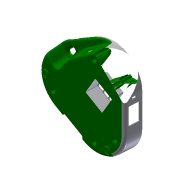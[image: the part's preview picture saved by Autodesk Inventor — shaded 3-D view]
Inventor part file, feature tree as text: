
AUTODESK INVENTOR PART (.ipt)
format: ipt  version: 2016 (Build 200138000, 138)  size: 3,453,440 bytes
history: native  units: in
note: dims shown in document units (in); Inventor stores cm internally (conversion verified against a paired STEP export)
features: extrude x9, sketch x8, projected_geometry x7, reference x5, fillet x3, chamfer x2, other x1, plane x1, pattern_linear x1, imported_body x1
ambient origin geometry x8: Origin, YZ Plane, XZ Plane, XY Plane, X Axis, Y Axis, Z Axis, Center Point
bodies: Solid1 (feature_tree), Solid2 (feature_tree)
feature tree (38):
  other  "bottom_cover-2016-04-29-21"
  sketch  "Sketch1"  dims[d0=0.0709in d1=0.0709in d2=0.3543in]
  plane  "Work Plane1"
  extrude  "Extrusion1"  Depth=0.0709in
  fillet  "Fillet1"  Radius=0.3543in
  extrude  "Extrusion2"  Depth=1.9685in
  extrude  "Extrusion3"  Depth=0.3937in
  extrude  "Extrusion4"  Depth=0.3937in TaperAngle=0.0deg
  chamfer  "Chamfer1"  Distance=3.937in
  chamfer  "Chamfer2"  Distance=0.5118in
  extrude  "Extrusion5"  Depth=0.1575in
  extrude  "Extrusion6"  Depth=0.1575in
  extrude  "Extrusion7"  Depth=0.1575in TaperAngle=30.0deg
  fillet  "Fillet2"  Radius=0.0787in
  pattern_linear  "Rectangular Pattern1"  Spacing1=0.0197in  [1 undecoded]
  fillet  "Fillet3"  Radius=5.9055in
  extrude  "Extrusion8"  TaperAngle=0.0deg  [1 undecoded]
  extrude  "Extrusion9"  TaperAngle=0.0deg  [1 undecoded]
  imported_body  "Base1"
  reference  "Reference1"
  reference  "Reference2"
  sketch  "Sketch6"  dims[d3=0.3543in d4=1.9685in]
  sketch  "Sketch7"  dims[d5=1.5748in d6=0.3937in d7=-0.0069in]
  projected_geometry  "Projected Loop1"
  projected_geometry  "Projected Loop2"
  sketch  "Sketch9"  dims[d8=0.1969in d9=0.3937in d10=0.0in d11=3.937in d12=0.0206in]
  reference  "Reference3"
  reference  "Reference4"
  reference  "Reference5"
  sketch  "Sketch10"  dims[d13=1.6535in]
  projected_geometry  "Projected Loop3"
  sketch  "Sketch11"  dims[d14=2.7559in]
  projected_geometry  "Projected Loop4"
  sketch  "Sketch13"  dims[d16=0.4331in]
  projected_geometry  "Projected Loop5"
  projected_geometry  "Projected Loop6"
  sketch  "Sketch14"  dims[d17=0.2165in d18=0.5118in d19=0.0787in d24=0.1969in d25=-0.0344in d26=0.0787in d27=0.0787in d28=30.0deg d29=0.0787in d30=0.0787in d31=30.0deg d32=0.0197in d33=5.9055in d35=0.0in d36=0.0in d37=3.3858in d38=3.3858in d39=0.2362in d40=0.0787in d41=1.9685in d42=-0.0069in d43=3.189in d44=3.189in d45=0.0787in d46=0.0787in d47=1.8504in d48=-0.0069in d49=0.1181in d50=0.1181in d51=0.9055in d52=0.9055in d53=2.7559in d54=-0.0069in d55=1.1811in d57=1.0236in d58=1.1811in d60=1.0236in d61=0.1181in d62=0.0787in d63=0.1575in d64=0.0394in d65=0.0344in d66=1.2205in d67=1.2205in d68=0.2559in d69=0.2559in d70=0.1575in d71=-0.0344in]
  projected_geometry  "Projected Loop7"
note: 3 required parameter values undecoded (feature->parameter linkage not recoverable at this tier; creation-order binding heuristic only, values carry confidence <= 0.55)
